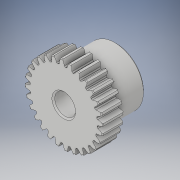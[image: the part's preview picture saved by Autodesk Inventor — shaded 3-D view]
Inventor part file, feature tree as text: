
AUTODESK INVENTOR PART (.ipt)
format: ipt  version: 2019 (Build 230136000, 136)  size: 543,744 bytes
history: native  units: in
note: dims shown in document units (in); Inventor stores cm internally (conversion verified against a paired STEP export)
features: chamfer x1
ambient origin geometry x8: Origin, YZ Plane, XZ Plane, XY Plane, X Axis, Y Axis, Z Axis, Center Point
bodies: Solid1 (feature_tree)
feature tree (1):
  chamfer  "Chamfer1"  [1 undecoded]
note: 1 required parameter value undecoded (feature->parameter linkage not recoverable at this tier; creation-order binding heuristic only, values carry confidence <= 0.55)
